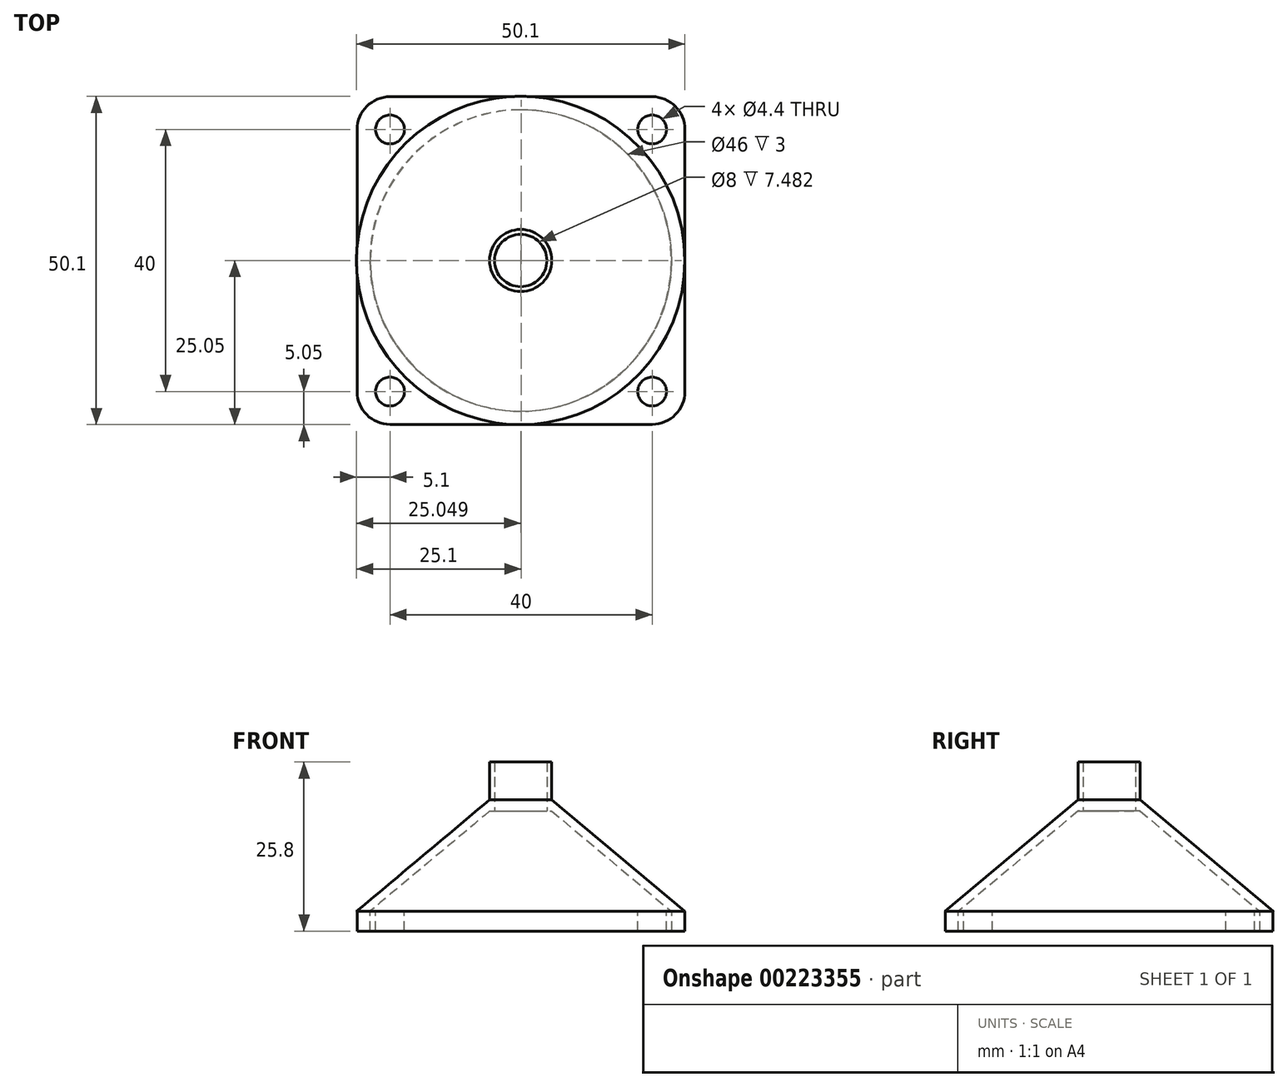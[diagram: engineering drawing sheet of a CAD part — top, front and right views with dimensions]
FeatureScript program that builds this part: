
annotation { "Feature Type Name" : "Feature", "Feature Type Description" : "" }
export const myFeature = defineFeature(function(context is Context, id is Id, definition is map)
    precondition{}
    {
        {
            var Q0;
            Q0=qCreatedBy(makeId("Front.planeOp"),FACE);
            var sketch = newSketch(context, id + "F0", { "sketchPlane" : qUnion([Q0])});
            skLineSegment(sketch, "E0.bottom", {"start": v(0, 0) * mm, "end": v(50, 0) * mm});
            skLineSegment(sketch, "E0.top", {"start": v(0, 3) * mm, "end": v(50, 3) * mm});
            skLineSegment(sketch, "E0.left", {"start": v(0, 0) * mm, "end": v(0, 3) * mm});
            skLineSegment(sketch, "E0.right", {"start": v(50, 0) * mm, "end": v(50, 3) * mm});
            skSolve(sketch);
        }
        {
            var Q0;
            Q0 = qSketchRegion(id + "F0", true);
            extrude(context, id + "F1", {"entities" : qUnion([Q0]), "oppositeDirection" : true, "depth" : 50 * mm});
        }
        {
            var Q0;
            Q0=makeQuery(id+"F1.opExtrude","SWEPT_FACE",FACE,{"disambiguationData":[OSD([sQuery(id+"F0.wireOp",EDGE,"E0.top")])]});
            var sketch = newSketch(context, id + "F2", { "sketchPlane" : qUnion([Q0])});
            skLineSegment(sketch, "E1", {"start": v(0, 25) * mm, "end": v(25, 25) * mm, "construction": true});
            skCircle(sketch, "E2", {"center": v(25, 25) * mm, "radius": 23 * mm});
            skSolve(sketch);
        }
        {
            var Q0;
            Q0 = qSketchRegion(id + "F2", true);
            extrude(context, id + "F3", {"entities" : qUnion([Q0]), "operationType" : NewBodyOperationType.REMOVE, "oppositeDirection" : true, "depth" : 25 * mm});
        }
        {
            var Q0;
            Q0=qCreatedBy(makeId("Front.planeOp"),FACE);
            cPlane(context, id + "F4", {"entities" : qUnion([Q0]), "cplaneType" : CPlaneType.OFFSET, "offset" : 25 * mm, "oppositeDirection" : true, "width" : 150 * mm, "height" : 150 * mm});
        }
        {
            var Q0;
            Q0=qCreatedBy(id+"F4.planeOp",FACE);
            var sketch = newSketch(context, id + "F5", { "sketchPlane" : qUnion([Q0])});
            skLineSegment(sketch, "E3", {"start": v(47.95, 3) * mm, "end": v(29.69, 18.32) * mm});
            skLineSegment(sketch, "E4", {"start": v(29.69, 18.32) * mm, "end": v(28.95, 18.32) * mm});
            skLineSegment(sketch, "E5", {"start": v(28.95, 18.32) * mm, "end": v(28.95, 25.8) * mm});
            skLineSegment(sketch, "E6", {"start": v(28.95, 25.8) * mm, "end": v(29.69, 25.8) * mm});
            skLineSegment(sketch, "E7", {"start": v(29.69, 25.8) * mm, "end": v(29.69, 20.04) * mm});
            skLineSegment(sketch, "E8", {"start": v(29.69, 20.04) * mm, "end": v(50, 3) * mm});
            skLineSegment(sketch, "E9", {"start": v(50, 3) * mm, "end": v(47.95, 3) * mm});
            skLineSegment(sketch, "E10", {"start": v(47.95, 3) * mm, "end": v(24.95, 3) * mm, "construction": true});
            skLineSegment(sketch, "E11", {"start": v(24.95, 3) * mm, "end": v(24.95, 25.71) * mm, "construction": true});
            skLineSegment(sketch, "E12", {"start": v(24.95, 25.71) * mm, "end": v(28.95, 25.8) * mm, "construction": true});
            skSolve(sketch);
        }
        {
            var Q0;
            Q0 = qSketchRegion(id + "F5", true);
            var Q1;
            Q1=sQuery(id+"F5.wireOp",EDGE,"E11");
            revolve(context, id + "F6", {"operationType" : NewBodyOperationType.ADD, "entities" : qUnion([Q0]), "axis" : qUnion([Q1]), "revolveType" : RevolveType.FULL});
        }
        {
            var Q0;
            {var subQ0=sQuery(id+"F0.wireOp",EDGE,"E0.left");var subQ1=sQuery(id+"F0.wireOp",EDGE,"E0.top");Q0=makeQuery(id+"F6.boolean.opBoolean","SPLIT",FACE,{"disambiguationData":[TD([makeQuery(id+"F1.opExtrude","CAP_FACE",FACE,{"disambiguationData":[OSD([sQuery(id+"F0.wireOp",EDGE,"E0.bottom"),subQ1,subQ0,sQuery(id+"F0.wireOp",EDGE,"E0.right")])],"isStart":false}),makeQuery(id+"F1.opExtrude","SWEPT_FACE",FACE,{"disambiguationData":[OSD([subQ0])]}),makeQuery(id+"F6.opRevolve","SWEPT_FACE",FACE,{"disambiguationData":[OSD([sQuery(id+"F5.wireOp",EDGE,"E8")])]}),makeQuery(id+"F6.opRevolve","SWEPT_FACE",FACE,{"disambiguationData":[OSD([sQuery(id+"F5.wireOp",EDGE,"E9")])]})])],"derivedFrom":makeQuery(id+"F1.opExtrude","SWEPT_FACE",FACE,{"disambiguationData":[OSD([subQ1])]})});}
            var sketch = newSketch(context, id + "F7", { "sketchPlane" : qUnion([Q0])});
            skCircle(sketch, "E13", {"center": v(5, 45) * mm, "radius": 2.2 * mm});
            skCircle(sketch, "E14", {"center": v(45, 45) * mm, "radius": 2.2 * mm});
            skCircle(sketch, "E15", {"center": v(45, 5) * mm, "radius": 2.2 * mm});
            skCircle(sketch, "E16", {"center": v(5, 5) * mm, "radius": 2.2 * mm});
            skLineSegment(sketch, "E17", {"start": v(5, 45) * mm, "end": v(5, 5) * mm, "construction": true});
            skLineSegment(sketch, "E18", {"start": v(5, 5) * mm, "end": v(45, 5) * mm, "construction": true});
            skLineSegment(sketch, "E19", {"start": v(45, 5) * mm, "end": v(45, 45) * mm, "construction": true});
            skLineSegment(sketch, "E20", {"start": v(45, 45) * mm, "end": v(5, 45) * mm, "construction": true});
            skLineSegment(sketch, "E21", {"start": v(5, 5) * mm, "end": v(0, 5) * mm, "construction": true});
            skLineSegment(sketch, "E22", {"start": v(45, 5) * mm, "end": v(50, 5) * mm, "construction": true});
            skLineSegment(sketch, "E23", {"start": v(5, 45) * mm, "end": v(5, 50) * mm, "construction": true});
            skLineSegment(sketch, "E24", {"start": v(5, 5) * mm, "end": v(5, 0) * mm, "construction": true});
            skSolve(sketch);
        }
        {
            var Q0;
            Q0=makeQuery(id+"F7.imprint","IMPRINT",FACE,{"disambiguationData":[TD([[makeQuery(id+"F7.imprint","IMPRINT",EDGE,{"derivedFrom":sQuery(id+"F7.wireOp",EDGE,"E14")}),1.0]])]});
            var Q1;
            Q1=makeQuery(id+"F7.imprint","IMPRINT",FACE,{"disambiguationData":[TD([[makeQuery(id+"F7.imprint","IMPRINT",EDGE,{"derivedFrom":sQuery(id+"F7.wireOp",EDGE,"E15")}),1.0]])]});
            var Q2;
            Q2=makeQuery(id+"F7.imprint","IMPRINT",FACE,{"disambiguationData":[TD([[makeQuery(id+"F7.imprint","IMPRINT",EDGE,{"derivedFrom":sQuery(id+"F7.wireOp",EDGE,"E16")}),1.0]])]});
            var Q3;
            Q3=makeQuery(id+"F7.imprint","IMPRINT",FACE,{"disambiguationData":[TD([[makeQuery(id+"F7.imprint","IMPRINT",EDGE,{"derivedFrom":sQuery(id+"F7.wireOp",EDGE,"E13")}),1.0]])]});
            extrude(context, id + "F8", {"entities" : qUnion([Q0, Q1, Q2, Q3]), "operationType" : NewBodyOperationType.REMOVE, "oppositeDirection" : true, "depth" : 25 * mm});
        }
        {
            var Q0;
            Q0=makeQuery(id+"F1.opExtrude","CAP_EDGE",EDGE,{"disambiguationData":[OSD([sQuery(id+"F0.wireOp",EDGE,"E0.left")])],"isStart":true});
            var Q1;
            Q1=makeQuery(id+"F1.opExtrude","CAP_EDGE",EDGE,{"disambiguationData":[OSD([sQuery(id+"F0.wireOp",EDGE,"E0.right")])],"isStart":true});
            var Q2;
            Q2=makeQuery(id+"F1.opExtrude","CAP_EDGE",EDGE,{"disambiguationData":[OSD([sQuery(id+"F0.wireOp",EDGE,"E0.right")])],"isStart":false});
            var Q3;
            Q3=makeQuery(id+"F1.opExtrude","CAP_EDGE",EDGE,{"disambiguationData":[OSD([sQuery(id+"F0.wireOp",EDGE,"E0.left")])],"isStart":false});
            fillet(context, id + "F9", {"entities" : qUnion([Q0, Q1, Q2, Q3]), "radius" : 5 * mm, "tangentPropagation" : true, "allowEdgeOverflow" : false});
        }
    });
